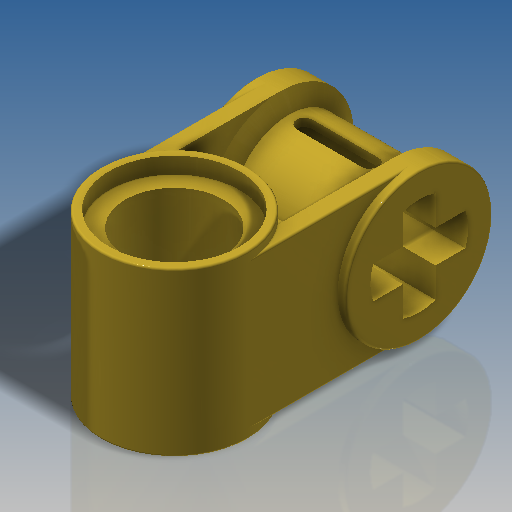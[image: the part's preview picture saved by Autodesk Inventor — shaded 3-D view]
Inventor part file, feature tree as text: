
AUTODESK INVENTOR PART (.ipt)
format: ipt  version: 2018.3 (Build 223284000, 284)  size: 344,576 bytes
history: native  units: in
note: dims shown in document units (in); Inventor stores cm internally (conversion verified against a paired STEP export)
features: extrude x6, sketch x4, mirror x1, plane x1, revolve x1, fillet x1
ambient origin geometry x8: Origin, YZ Plane, XZ Plane, XY Plane, X Axis, Y Axis, Z Axis, Center Point
bodies: Solid1 (feature_tree)
feature tree (14):
  sketch  "Sketch2"  dims[d0=0.2835in d1=0.189in]
  extrude  "Extrusion1"  Depth=0.189in
  extrude  "Extrusion3"  Depth=0.315in TaperAngle=0.0deg
  mirror  "Mirror1"
  plane  "Work Plane1"
  extrude  "Extrusion2"  Depth=0.2835in
  revolve  "Revolution1"  [1 undecoded]
  extrude  "Extrusion4"  Depth=0.0039in
  extrude  "Extrusion5"  Depth=0.0039in TaperAngle=0.0deg
  extrude  "Extrusion6"  Depth=0.0039in
  fillet  "Fillet1"  Radius=0.0472in
  sketch  "Sketch3"  dims[d2=0.315in d3=0.315in d4=0.0in]
  sketch  "Sketch4"  dims[d5=0.0in d6=0.2835in]
  sketch  "Sketch5"  dims[d7=0.0315in d8=0.315in d9=0.0in d10=0.252in d11=0.0315in d12=0.0in d13=0.2835in d14=0.0472in d15=0.315in d16=0.2205in d17=0.063in d18=0.0315in d19=0.1575in d20=90.0deg d21=0.063in d22=0.0in d23=0.063in d24=0.0in d25=0.189in d26=0.063in d27=0.063in d28=0.0in d29=0.0039in]
note: 1 required parameter value undecoded (feature->parameter linkage not recoverable at this tier; creation-order binding heuristic only, values carry confidence <= 0.55)
